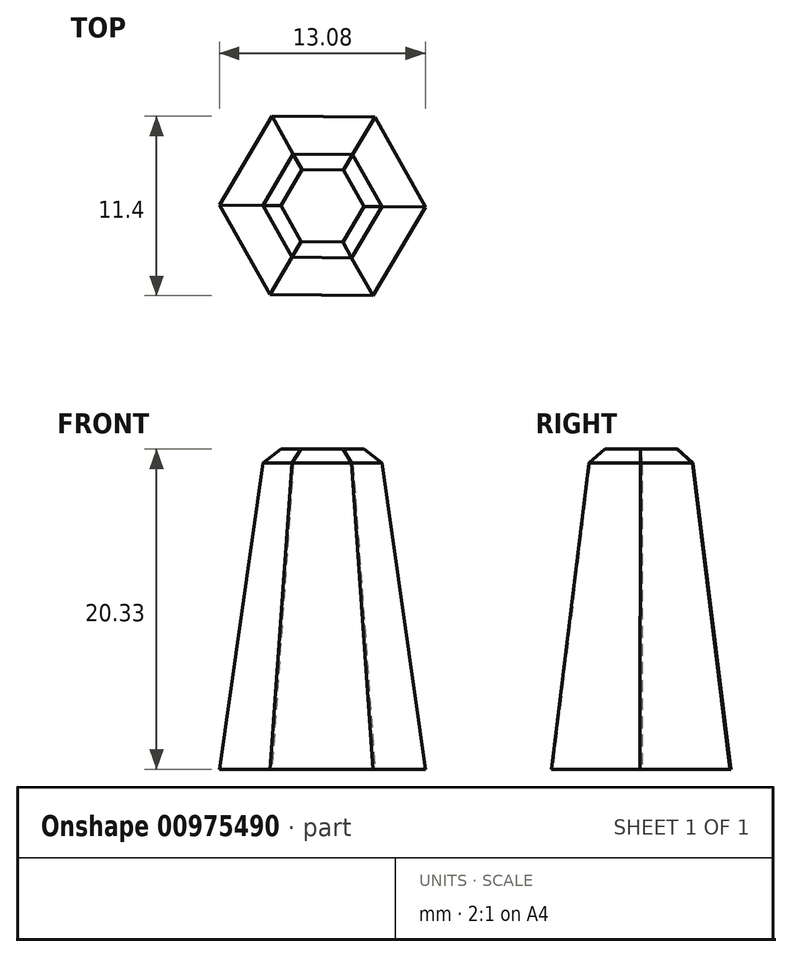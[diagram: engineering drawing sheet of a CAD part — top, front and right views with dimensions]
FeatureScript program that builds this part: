
annotation { "Feature Type Name" : "Feature", "Feature Type Description" : "" }
export const myFeature = defineFeature(function(context is Context, id is Id, definition is map)
    precondition{}
    {
        {
            var Q0;
            Q0=qCreatedBy(makeId("Top.planeOp"),FACE);
            var sketch = newSketch(context, id + "F0", { "sketchPlane" : qUnion([Q0])});
            skCircle(sketch, "E0.cCircle", {"center": v(0, 0) * mm, "radius": 5.67 * mm, "construction": true});
            skLineSegment(sketch, "E0.0", {"start": v(6.54, -0.07) * mm, "end": v(3.21, -5.7) * mm});
            skLineSegment(sketch, "E0.1", {"start": v(3.21, -5.7) * mm, "end": v(-3.33, -5.63) * mm});
            skLineSegment(sketch, "E0.2", {"start": v(-3.33, -5.63) * mm, "end": v(-6.54, 0.07) * mm});
            skLineSegment(sketch, "E0.3", {"start": v(-6.54, 0.07) * mm, "end": v(-3.21, 5.7) * mm});
            skLineSegment(sketch, "E0.4", {"start": v(-3.21, 5.7) * mm, "end": v(3.33, 5.63) * mm});
            skLineSegment(sketch, "E0.5", {"start": v(3.33, 5.63) * mm, "end": v(6.54, -0.07) * mm});
            skPoint(sketch, "E0.0.midPoint", {"position": v(4.88, -2.89) * mm});
            skSolve(sketch);
        }
        {
            var Q0;
            Q0=makeQuery(id+"F0.imprint","IMPRINT",FACE,{"disambiguationData":[TD([[makeQuery(id+"F0.imprint","IMPRINT",EDGE,{"derivedFrom":sQuery(id+"F0.wireOp",EDGE,"E0.0")}),-1.0]])]});
            extrude(context, id + "F1", {"entities" : qUnion([Q0]), "depth" : 20.33 * mm, "offsetDistance" : 25 * mm, "hasDraft" : true, "draftAngle" : 7 * degree, "draftPullDirection" : true});
        }
        {
            var Q0;
            Q0=makeQuery(id+"F1.opExtrude","CAP_EDGE",EDGE,{"disambiguationData":[OSD([sQuery(id+"F0.wireOp",EDGE,"E0.5")])],"isStart":false});
            var Q1;
            Q1=makeQuery(id+"F1.opExtrude","CAP_EDGE",EDGE,{"disambiguationData":[OSD([sQuery(id+"F0.wireOp",EDGE,"E0.2")])],"isStart":false});
            var Q2;
            Q2=makeQuery(id+"F1.opExtrude","CAP_EDGE",EDGE,{"disambiguationData":[OSD([sQuery(id+"F0.wireOp",EDGE,"E0.4")])],"isStart":false});
            var Q3;
            Q3=makeQuery(id+"F1.opExtrude","CAP_EDGE",EDGE,{"disambiguationData":[OSD([sQuery(id+"F0.wireOp",EDGE,"E0.3")])],"isStart":false});
            var Q4;
            Q4=makeQuery(id+"F1.opExtrude","CAP_EDGE",EDGE,{"disambiguationData":[OSD([sQuery(id+"F0.wireOp",EDGE,"E0.1")])],"isStart":false});
            var Q5;
            Q5=makeQuery(id+"F1.opExtrude","CAP_EDGE",EDGE,{"disambiguationData":[OSD([sQuery(id+"F0.wireOp",EDGE,"E0.0")])],"isStart":false});
            chamfer(context, id + "F2", {"entities" : qUnion([Q0, Q1, Q2, Q3, Q4, Q5]), "width" : 1 * mm, "tangentPropagation" : true});
        }
    });
